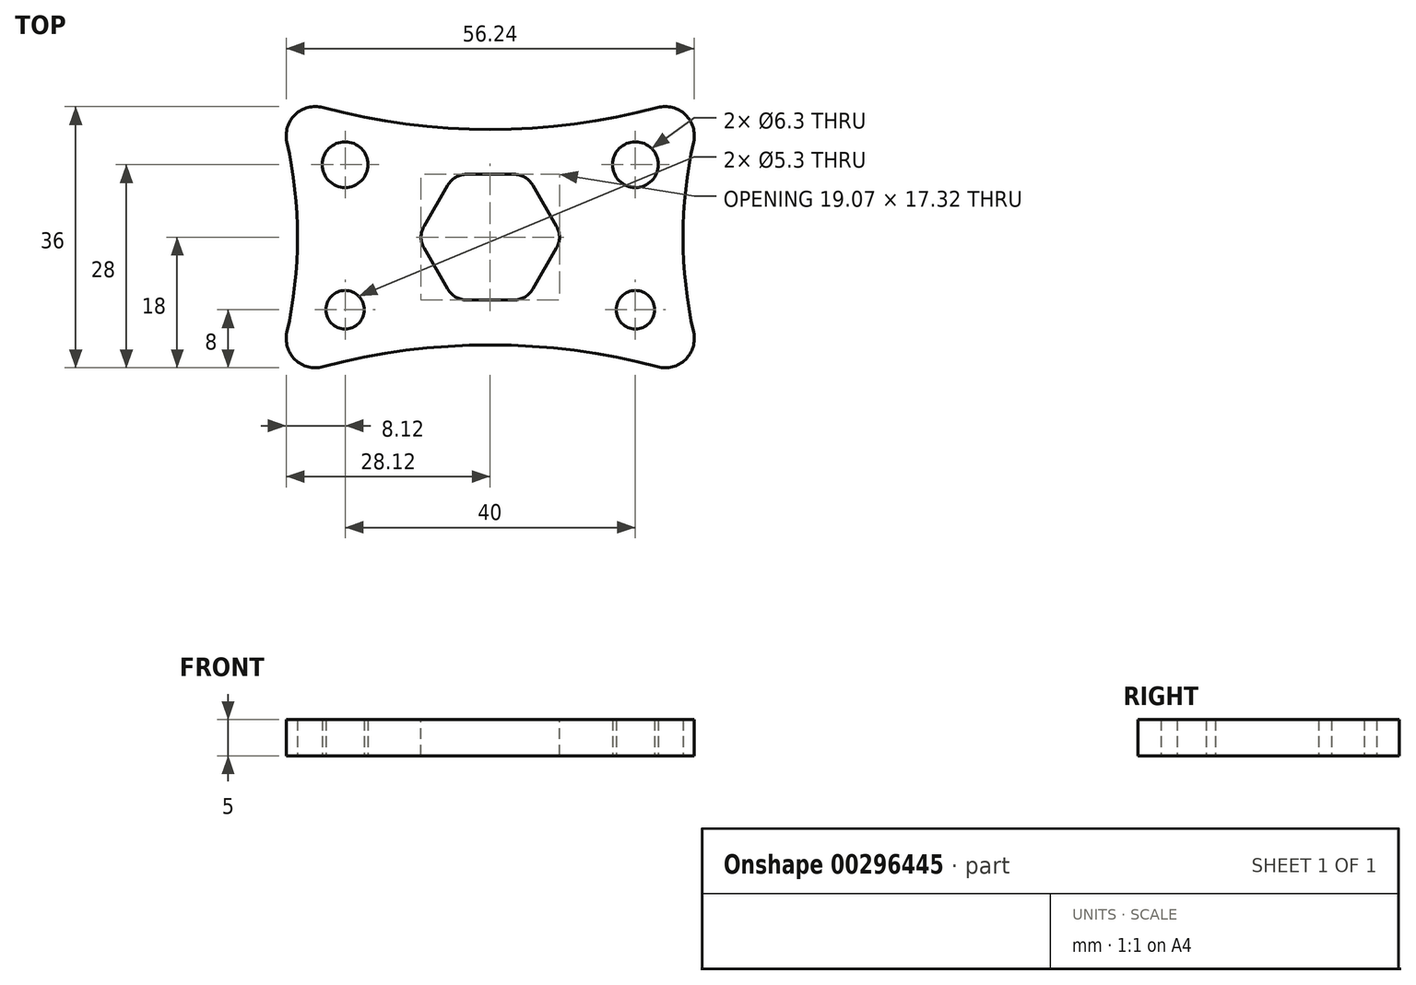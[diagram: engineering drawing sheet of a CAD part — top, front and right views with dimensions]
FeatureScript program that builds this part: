
annotation { "Feature Type Name" : "Feature", "Feature Type Description" : "" }
export const myFeature = defineFeature(function(context is Context, id is Id, definition is map)
    precondition{}
    {
        {
            var Q0;
            Q0=qCreatedBy(makeId("Top.planeOp"),FACE);
            var sketch = newSketch(context, id + "F0", { "sketchPlane" : qUnion([Q0])});
            skLineSegment(sketch, "E0.bottom", {"start": v(30, -20) * mm, "end": v(-30, -20) * mm, "construction": true});
            skLineSegment(sketch, "E0.top", {"start": v(30, 20) * mm, "end": v(-30, 20) * mm, "construction": true});
            skLineSegment(sketch, "E0.left", {"start": v(30, -20) * mm, "end": v(30, 20) * mm, "construction": true});
            skLineSegment(sketch, "E0.right", {"start": v(-30, -20) * mm, "end": v(-30, 20) * mm, "construction": true});
            skPoint(sketch, "E0.middle", {"position": v(0, 0) * mm});
            skArc(sketch, "E1", {"start": v(30, -20) * mm, "mid": v(0, -14.85) * mm, "end": v(-30, -20) * mm});
            skLineSegment(sketch, "E2", {"start": v(-30, 0) * mm, "end": v(30, 0) * mm, "construction": true});
            skLineSegment(sketch, "E3", {"start": v(-10, 20) * mm, "end": v(-10, -20) * mm, "construction": true});
            skLineSegment(sketch, "E4.MirrorCS", {"start": v(10, 20) * mm, "end": v(10, -20) * mm, "construction": true});
            skArc(sketch, "E5.MirrorCS", {"start": v(30, 20) * mm, "mid": v(0, 14.85) * mm, "end": v(-30, 20) * mm});
            skArc(sketch, "E6", {"start": v(30, 20) * mm, "mid": v(26.57, 0) * mm, "end": v(30, -20) * mm});
            skArc(sketch, "E7.MirrorCS", {"start": v(-30, 20) * mm, "mid": v(-26.57, 0) * mm, "end": v(-30, -20) * mm});
            skLineSegment(sketch, "E8", {"start": v(-10, 0) * mm, "end": v(-30, -20) * mm, "construction": true});
            skLineSegment(sketch, "E9", {"start": v(30, 0) * mm, "end": v(10, -20) * mm, "construction": true});
            skLineSegment(sketch, "E10", {"start": v(-30, 10) * mm, "end": v(-10, 10) * mm, "construction": true});
            skLineSegment(sketch, "E11.MirrorCS", {"start": v(30, 10) * mm, "end": v(10, 10) * mm, "construction": true});
            skCircle(sketch, "E12", {"center": v(-20, -10) * mm, "radius": 2.65 * mm});
            skCircle(sketch, "E13.MirrorC", {"center": v(20, -10) * mm, "radius": 2.65 * mm});
            skCircle(sketch, "E14", {"center": v(-20, 10) * mm, "radius": 3.15 * mm});
            skCircle(sketch, "E15.MirrorC", {"center": v(20, 10) * mm, "radius": 3.15 * mm});
            skCircle(sketch, "E16.cCircle", {"center": v(0, 0) * mm, "radius": 8.66 * mm, "construction": true});
            skLineSegment(sketch, "E16.0", {"start": v(5, -8.66) * mm, "end": v(-5, -8.66) * mm});
            skLineSegment(sketch, "E16.1", {"start": v(-5, -8.66) * mm, "end": v(-10, 0) * mm});
            skLineSegment(sketch, "E16.2", {"start": v(-10, 0) * mm, "end": v(-5, 8.66) * mm});
            skLineSegment(sketch, "E16.3", {"start": v(-5, 8.66) * mm, "end": v(5, 8.66) * mm});
            skLineSegment(sketch, "E16.4", {"start": v(5, 8.66) * mm, "end": v(10, 0) * mm});
            skLineSegment(sketch, "E16.5", {"start": v(10, 0) * mm, "end": v(5, -8.66) * mm});
            skPoint(sketch, "E16.0.midPoint", {"position": v(0, -8.66) * mm});
            skSolve(sketch);
        }
        {
            var Q0;
            Q0=makeQuery(id+"F0.imprint","IMPRINT",FACE,{"disambiguationData":[TD([[makeQuery(id+"F0.imprint","IMPRINT",EDGE,{"derivedFrom":sQuery(id+"F0.wireOp",EDGE,"E1")}),-1.0]])]});
            extrude(context, id + "F1", {"entities" : qUnion([Q0]), "depth" : 5 * mm});
        }
        {
            var Q0;
            Q0=makeQuery(id+"F1.opExtrude","SWEPT_EDGE",EDGE,{"disambiguationData":[OSD([sQuery(id+"F0.wireOp",EDGE,"E5.MirrorCS"),sQuery(id+"F0.wireOp",EDGE,"E6")])]});
            var Q1;
            Q1=makeQuery(id+"F1.opExtrude","SWEPT_EDGE",EDGE,{"disambiguationData":[OSD([sQuery(id+"F0.wireOp",EDGE,"E5.MirrorCS"),sQuery(id+"F0.wireOp",EDGE,"E7.MirrorCS")])]});
            var Q2;
            Q2=makeQuery(id+"F1.opExtrude","SWEPT_EDGE",EDGE,{"disambiguationData":[OSD([sQuery(id+"F0.wireOp",EDGE,"E1"),sQuery(id+"F0.wireOp",EDGE,"E7.MirrorCS")])]});
            var Q3;
            Q3=makeQuery(id+"F1.opExtrude","SWEPT_EDGE",EDGE,{"disambiguationData":[OSD([sQuery(id+"F0.wireOp",EDGE,"E1"),sQuery(id+"F0.wireOp",EDGE,"E6")])]});
            fillet(context, id + "F2", {"entities" : qUnion([Q0, Q1, Q2, Q3]), "radius" : 4 * mm, "tangentPropagation" : true, "allowEdgeOverflow" : false});
        }
        {
            var Q0;
            Q0=makeQuery(id+"F1.opExtrude","SWEPT_EDGE",EDGE,{"disambiguationData":[OSD([sQuery(id+"F0.wireOp",EDGE,"E16.3"),sQuery(id+"F0.wireOp",EDGE,"E16.4")])]});
            var Q1;
            Q1=makeQuery(id+"F1.opExtrude","SWEPT_EDGE",EDGE,{"disambiguationData":[OSD([sQuery(id+"F0.wireOp",EDGE,"E16.2"),sQuery(id+"F0.wireOp",EDGE,"E16.3")])]});
            var Q2;
            Q2=makeQuery(id+"F1.opExtrude","SWEPT_EDGE",EDGE,{"disambiguationData":[OSD([sQuery(id+"F0.wireOp",EDGE,"E16.4"),sQuery(id+"F0.wireOp",EDGE,"E16.5")])]});
            var Q3;
            Q3=makeQuery(id+"F1.opExtrude","SWEPT_EDGE",EDGE,{"disambiguationData":[OSD([sQuery(id+"F0.wireOp",EDGE,"E16.0"),sQuery(id+"F0.wireOp",EDGE,"E16.5")])]});
            var Q4;
            Q4=makeQuery(id+"F1.opExtrude","SWEPT_EDGE",EDGE,{"disambiguationData":[OSD([sQuery(id+"F0.wireOp",EDGE,"E16.0"),sQuery(id+"F0.wireOp",EDGE,"E16.1")])]});
            var Q5;
            Q5=makeQuery(id+"F1.opExtrude","SWEPT_EDGE",EDGE,{"disambiguationData":[OSD([sQuery(id+"F0.wireOp",EDGE,"E16.1"),sQuery(id+"F0.wireOp",EDGE,"E16.2")])]});
            fillet(context, id + "F3", {"entities" : qUnion([Q0, Q1, Q2, Q3, Q4, Q5]), "radius" : 3 * mm, "tangentPropagation" : true, "allowEdgeOverflow" : false});
        }
    });
